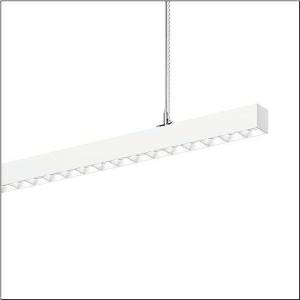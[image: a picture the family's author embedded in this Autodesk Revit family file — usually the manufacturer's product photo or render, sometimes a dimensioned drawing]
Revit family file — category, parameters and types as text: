
# Revit family: silica_r__21_51mx36dc3dwb_b05b
name_source: partatom
category: Lighting Fixtures
units: mm (PartAtom-declared; Revit-internal decimal feet)

## family parameters
Cut with Voids When Loaded = No
Host = Face
Light Source = No
Part Type = Normal
Room Calculation Point = No
Round Connector Dimension = Use Diameter
Shared = No

## types (1)
- --- (1 x LED, 17650 lm, 104.1 W, 3000K)
    Apparent Load = 104 VA
    CIE Flux Codes = 83 98 100 61 100
    Color Rendering = 80
    Color Temperature = 3000K
    Default Elevation = 1800 mm
    Description = Silica® 21, office luminaire, primary light control with darklight reflector, of PMMA, white, CAT 2 (L<= 3000cd/m²), light emission: direct/indirect distribution, primary light characteristic: symmetric, installation type: suspended mounting, LED, rated luminous flux: 17.650lm, luminous efficacy: 170lm/W, light colour: 830, colour temperature: 3000K, control gear: DALI 2, with terminal, 3+2-pole, max. 2.5mm², mains connection: 220..240V, AC, 50/60Hz, rated input power: 104.1W, luminaire housing, of aluminium, traffic white (RAL 9016), length: 3.004mm, width: 53mm, height: 53mm, protection rating (complete): IP20, insulation class (complete): insulation class I (protective earthing), certification: CE, permissible operating ambient temperature: 0..+35°C, standard: EN 50419, packaging unit: 1 piece
    Height = 53 mm
    Lamp = 1 x LED
    Lamp Light Flux = 17650 lm
    Lamp Power = 104.1 W
    Lamp count = 1
    Length = 3004 mm
    Luminous efficacy = 170 lm/W
    Manufacturer = Siteco
    ModVariant = No
    Model = 51MX36DC3DWB
    Mounting Place = Ceiling
    Mounting Type = Pendant
    Number of Poles = 1
    OnlyDefault = Yes
    Power Factor = 1
    Product Name = Silica® 21
    Product group = office luminaire | ceiling pendant
    ProductGroupID = 904
    Protection Class = Protection class I
    Protection Degree = IP 20
    RLX_Detail_Level = 1
    RLX_Emergency_Light_Flux = 0 lm
    RLX_Emergency_Type = 0
    RLX_Emergency_Type_DB = No
    RlxData = <blob elided: 61669 chars, md5=5f581f1d>
    Socket = socket
    Standby Power = 0 W
    System Light Flux = 17650 lm
    System Power = 104 W
    Type Comments = factory setting: luminous flux: 100 % | dim-lin: 254 | 359 mA
    Type Image = l_1335921.jpg
    URL = http://relux.com
    VarID = @adj_121438
    Voltage = 0 V
    Weight = 0.00 kg
    Width = 53 mm

## geometry (parser evidence)
native form markers: Blend x4, Sweep x12
no freeform markers — native parametric forms only
